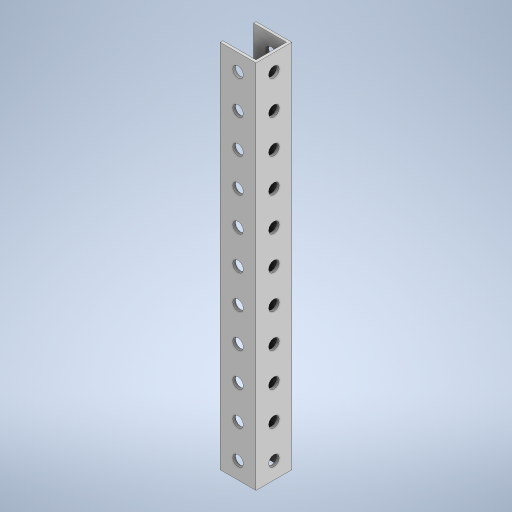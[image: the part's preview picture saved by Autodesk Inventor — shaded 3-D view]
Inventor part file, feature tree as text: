
AUTODESK INVENTOR PART (.ipt)
format: ipt  version: 2024 (Build 280153020, 153B)  size: 288,256 bytes
history: native  units: in
note: dims shown in document units (in); Inventor stores cm internally (conversion verified against a paired STEP export)
features: extrude x3, sketch x3, pattern_linear x1
ambient origin geometry x8: Origin, YZ Plane, XZ Plane, XY Plane, X Axis, Y Axis, Z Axis, Center Point
bodies: Solid1 (feature_tree)
feature tree (7):
  extrude  "Extrusion1"  Depth=1.063in
  sketch  "Sketch2"  dims[d2=0.0787in d3=11.0in d4=0.0in]
  sketch  "Sketch3"  dims[d5=0.5in d6=0.315in d7=0.5in d8=0.315in d9=3.6688in d10=0.0in d11=4.6437in d12=0.0in d13=4.3307in d15=1.0in]
  extrude  "Extrusion2"  Depth=11.0in TaperAngle=0.0deg
  extrude  "Extrusion3"  Depth=0.315in
  pattern_linear  "Rectangular Pattern1"  Spacing1=0.5in  [1 undecoded]
  sketch  "Sketch1"  dims[d0=1.063in d1=1.063in]
note: 1 required parameter value undecoded (feature->parameter linkage not recoverable at this tier; creation-order binding heuristic only, values carry confidence <= 0.55)
